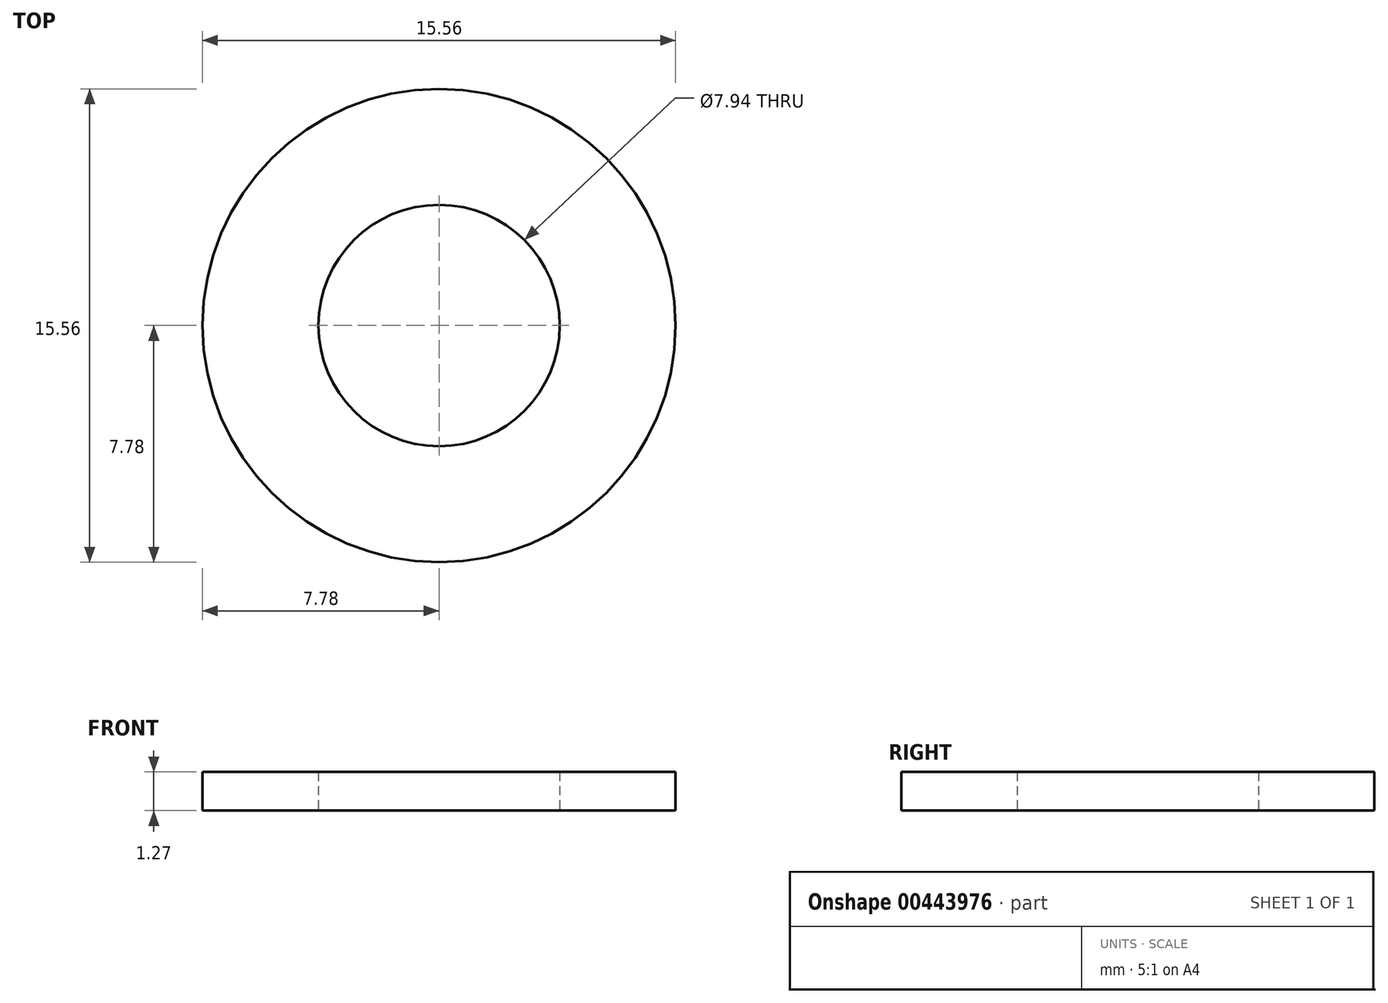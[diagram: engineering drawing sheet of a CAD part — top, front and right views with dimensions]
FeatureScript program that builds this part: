
annotation { "Feature Type Name" : "Feature", "Feature Type Description" : "" }
export const myFeature = defineFeature(function(context is Context, id is Id, definition is map)
    precondition{}
    {
        {
            var Q0;
            Q0=qCreatedBy(makeId("Top.planeOp"),FACE);
            var sketch = newSketch(context, id + "F0", { "sketchPlane" : qUnion([Q0])});
            skCircle(sketch, "E0", {"center": v(0, 0) * mm, "radius": 3.97 * mm});
            skCircle(sketch, "E1.0", {"center": v(0, 0) * mm, "radius": 7.78 * mm});
            skSolve(sketch);
        }
        {
            var Q0;
            Q0=makeQuery(id+"F0.imprint","IMPRINT",FACE,{"disambiguationData":[TD([[makeQuery(id+"F0.imprint","IMPRINT",EDGE,{"derivedFrom":sQuery(id+"F0.wireOp",EDGE,"E0")}),-1.0]])]});
            extrude(context, id + "F1", {"entities" : qUnion([Q0]), "depth" : 1.27 * mm});
        }
    });
